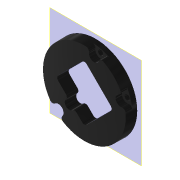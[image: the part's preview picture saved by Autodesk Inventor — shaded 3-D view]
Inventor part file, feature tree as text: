
AUTODESK INVENTOR PART (.ipt)
format: ipt  version: 2022 (Build 260153000, 153)  size: 242,176 bytes
history: native  units: in
note: dims shown in document units (in); Inventor stores cm internally (conversion verified against a paired STEP export)
features: reference x9, other x7, sketch x2, plane x1, extrude x1, hole x1, fillet x1
ambient origin geometry x8: Origin, YZ Plane, XZ Plane, XY Plane, X Axis, Y Axis, Z Axis, Center Point
bodies: Solid1 (feature_tree)
feature tree (22):
  plane  "Work Plane1"
  extrude  "Extrusion1"  Depth=0.9843in
  hole  "Bohrung1"  [1 undecoded]
  fillet  "Rundung1"  [1 undecoded]
  sketch  "Sketch1"  dims[d0=0.2756in d1=-0.0069in]
  reference  "Reference1"
  reference  "Reference5"
  reference  "Reference6"
  reference  "Reference7"
  sketch  "Skizze4"  dims[d9=0.126in d10=0.75in d11=0.2559in d12=0.1575in d13=0.5635in d14=1.0in d15=0.8108in d17=0.9843in d18=0.9843in d19=45.0deg d20=0.9843in d21=0.0787in d22=0.0787in]
  reference  "Referenz9"
  reference  "Referenz10"
  reference  "Referenz11"
  reference  "Referenz12"
  reference  "Referenz13"
  other  "<userpath>\Documents\Matchboxscope\INVENTOR\Matchboxscope_v1.iam"
  other  "Matchboxscope_v1.iam"
  other  "Matchboxscope_middle2_v1:1"
  other  "Matchboxscope_VCM_v1.iam"
  other  "Matchboxscope_middle2_m12VCMLens_v2:1"
  other  "Baugruppe1"
  other  "IM_Matchboxscope_base:1"
note: 2 required parameter values undecoded (feature->parameter linkage not recoverable at this tier; creation-order binding heuristic only, values carry confidence <= 0.55)
